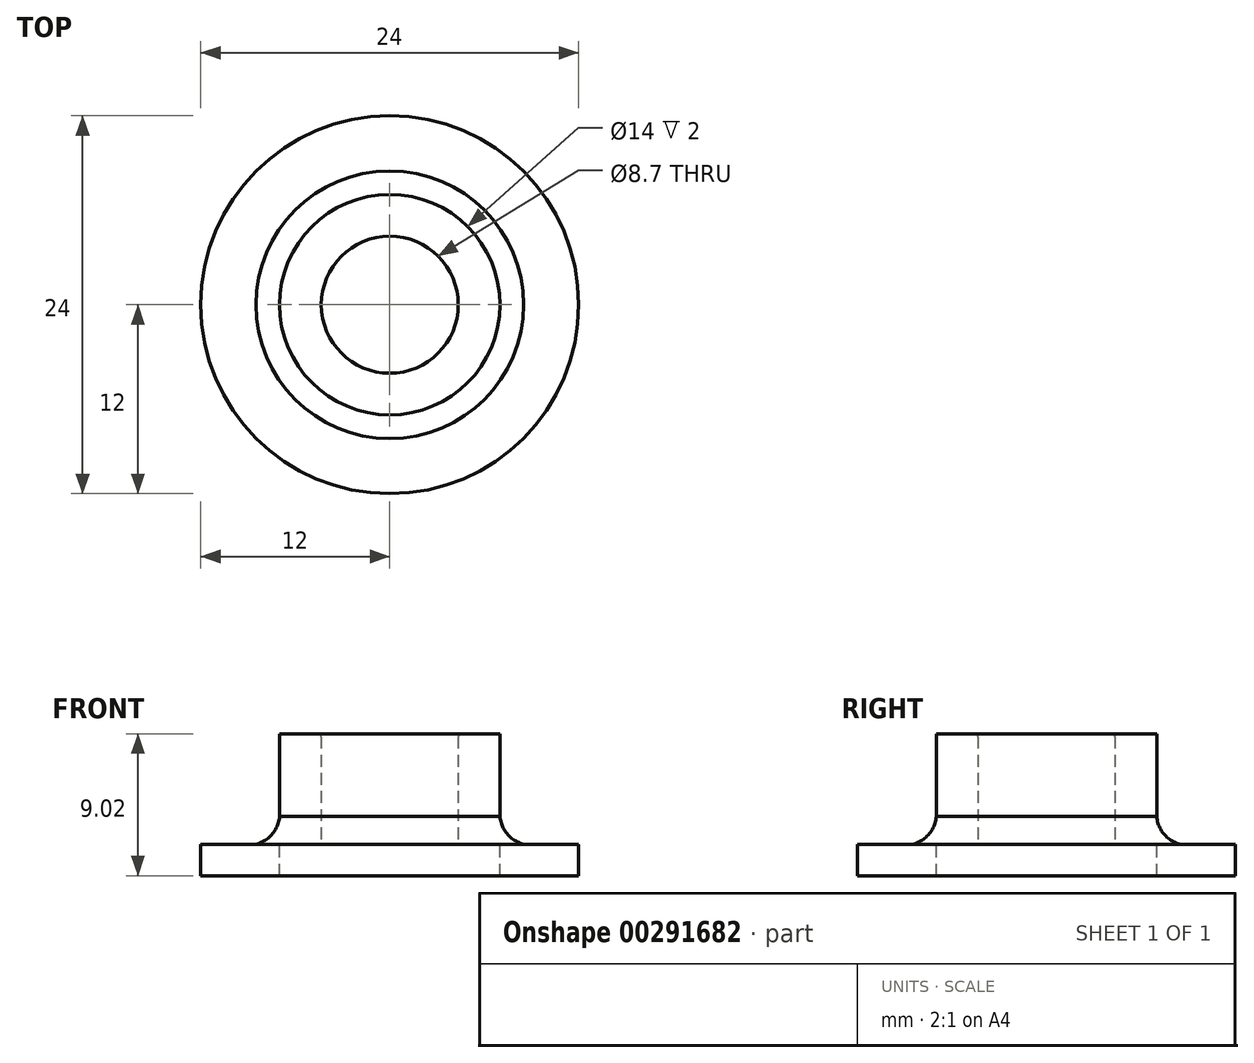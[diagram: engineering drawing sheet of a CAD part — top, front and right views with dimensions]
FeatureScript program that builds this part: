
annotation { "Feature Type Name" : "Feature", "Feature Type Description" : "" }
export const myFeature = defineFeature(function(context is Context, id is Id, definition is map)
    precondition{}
    {
        {
            var Q0;
            Q0=qCreatedBy(makeId("Top.planeOp"),FACE);
            var sketch = newSketch(context, id + "F0", { "sketchPlane" : qUnion([Q0])});
            skCircle(sketch, "E0", {"center": v(0, 0) * mm, "radius": 12 * mm});
            skCircle(sketch, "E1", {"center": v(0, 0) * mm, "radius": 7 * mm});
            skCircle(sketch, "E2", {"center": v(0, 0) * mm, "radius": 4.35 * mm});
            skSolve(sketch);
        }
        {
            var Q0;
            Q0=makeQuery(id+"F0.imprint","IMPRINT",FACE,{"disambiguationData":[TD([[makeQuery(id+"F0.imprint","IMPRINT",EDGE,{"derivedFrom":sQuery(id+"F0.wireOp",EDGE,"E0")}),1.0]])]});
            extrude(context, id + "F1", {"entities" : qUnion([Q0]), "oppositeDirection" : true, "depth" : 2 * mm});
        }
        {
            var Q0;
            Q0=makeQuery(id+"F0.imprint","IMPRINT",FACE,{"disambiguationData":[TD([[makeQuery(id+"F0.imprint","IMPRINT",EDGE,{"derivedFrom":sQuery(id+"F0.wireOp",EDGE,"E1")}),1.0]])]});
            extrude(context, id + "F2", {"entities" : qUnion([Q0]), "depth" : 7.02 * mm});
        }
        {
            var Q0;
            Q0=makeQuery(id+"F0.imprint","IMPRINT",FACE,{"disambiguationData":[TD([[makeQuery(id+"F0.imprint","IMPRINT",EDGE,{"derivedFrom":sQuery(id+"F0.wireOp",EDGE,"E0")}),1.0]])]});
            var sketch = newSketch(context, id + "F3", { "sketchPlane" : qUnion([Q0])});
            skCircle(sketch, "E3", {"center": v(0, 0) * mm, "radius": 8.5 * mm});
            skSolve(sketch);
        }
        {
            var Q0;
            Q0=makeQuery(id+"F0.imprint","IMPRINT",FACE,{"disambiguationData":[TD([[makeQuery(id+"F0.imprint","IMPRINT",EDGE,{"derivedFrom":sQuery(id+"F0.wireOp",EDGE,"E0")}),1.0]])]});
            cPlane(context, id + "F4", {"entities" : qUnion([Q0]), "cplaneType" : CPlaneType.OFFSET, "offset" : 2.12 * mm, "width" : 150 * mm, "height" : 150 * mm});
        }
        {
            var Q0;
            Q0=qCreatedBy(id+"F4.planeOp",FACE);
            var sketch = newSketch(context, id + "F5", { "sketchPlane" : qUnion([Q0])});
            skCircle(sketch, "E4", {"center": v(0, 0) * mm, "radius": 7 * mm});
            skSolve(sketch);
        }
        {
            var Q0;
            Q0=qCreatedBy(makeId("Front.planeOp"),FACE);
            var sketch = newSketch(context, id + "F6", { "sketchPlane" : qUnion([Q0])});
            skLineSegment(sketch, "E5", {"start": v(0, 0) * mm, "end": v(0, 11.27) * mm, "construction": true});
            skArc(sketch, "E6", {"start": v(-8.5, 0) * mm, "mid": v(-7.36, 0.78) * mm, "end": v(-7, 2.12) * mm});
            skLineSegment(sketch, "E7", {"start": v(-7, 2.12) * mm, "end": v(-7, 0) * mm});
            skLineSegment(sketch, "E8", {"start": v(-7, 0) * mm, "end": v(-8.5, 0) * mm});
            skSolve(sketch);
        }
        {
            var Q0;
            {var subQ0=sQuery(id+"F6.wireOp",EDGE,"E8");Q0=makeQuery(id+"F6.imprint","IMPRINT",FACE,{"disambiguationData":[TD([[makeQuery(id+"F6.imprint","IMPRINT",EDGE,{"derivedFrom":subQ0}),-1.0]])]});}
            var Q1;
            Q1=sQuery(id+"F6.wireOp",EDGE,"E5");
            revolve(context, id + "F7", {"operationType" : NewBodyOperationType.ADD, "entities" : qUnion([Q0]), "axis" : qUnion([Q1]), "revolveType" : RevolveType.FULL});
        }
        {
            var Q0;
            Q0=makeQuery(id+"F2.opExtrude","CAP_EDGE",EDGE,{"disambiguationData":[OSD([sQuery(id+"F0.wireOp",EDGE,"E2")])],"isStart":false});
            fillet(context, id + "F8", {"entities" : qUnion([Q0]), "tangentPropagation" : true, "radius" : 0.2 * mm, "defaultsChanged" : true, "vertexSettings" : [], "allowEdgeOverflow" : false});
        }
    });
